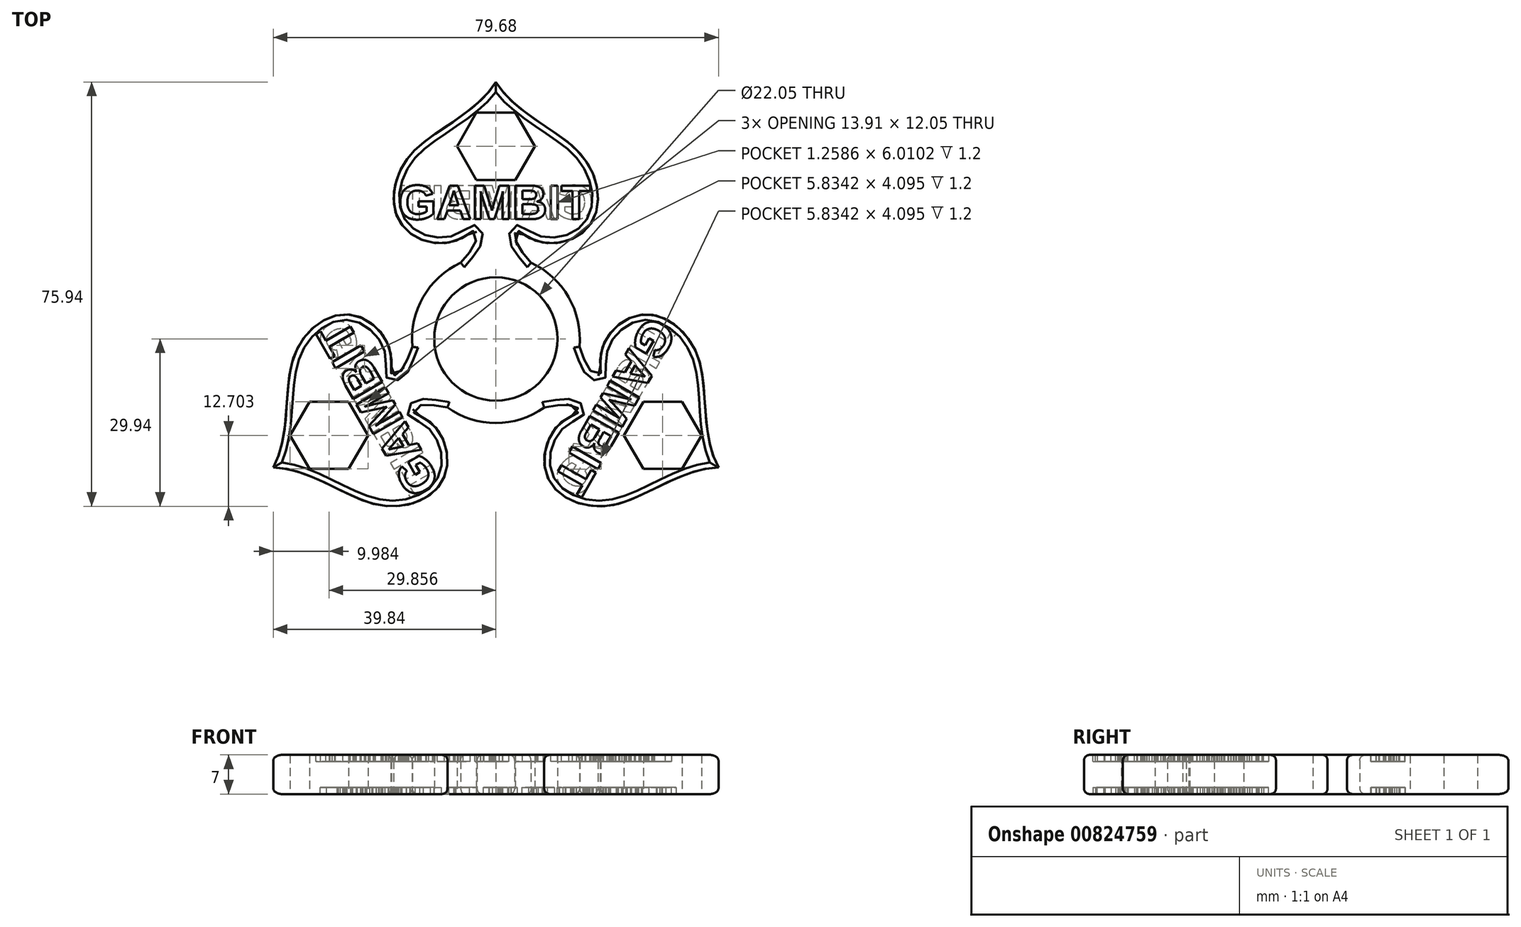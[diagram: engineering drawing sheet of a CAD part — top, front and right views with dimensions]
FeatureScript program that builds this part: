
annotation { "Feature Type Name" : "Feature", "Feature Type Description" : "" }
export const myFeature = defineFeature(function(context is Context, id is Id, definition is map)
    precondition{}
    {
        {
            var Q0;
            Q0=qCreatedBy(makeId("Top.planeOp"),FACE);
            var sketch = newSketch(context, id + "F0", { "sketchPlane" : qUnion([Q0])});
            skCircle(sketch, "E0", {"center": v(0, 0) * mm, "radius": 11.03 * mm});
            skCircle(sketch, "E1", {"center": v(0, 0) * mm, "radius": 15.03 * mm});
            skCircle(sketch, "E2", {"center": v(0, 0) * mm, "radius": 46 * mm, "construction": true});
            skLineSegment(sketch, "E3", {"start": v(0, 0) * mm, "end": v(0, 50.77) * mm, "construction": true});
            skFitSpline(sketch, "E4", {"points": [v(-6.29, 13.65) * mm, v(-3.78, 16.83) * mm, v(-3.57, 19.36) * mm, v(-6.6, 17.8) * mm, v(-13.45, 17.85) * mm, v(-17.97, 22.72) * mm, v(-15.15, 33.11) * mm, v(0, 46) * mm], "startDerivative": vector(35.72, 51.03) * mm, "endDerivative": vector(43.67, 71.8) * mm});
            skCircle(sketch, "E5", {"center": v(-9.97, 25.6) * mm, "radius": 8.5 * mm, "construction": true});
            skFitSpline(sketch, "E6.MirrorCS", {"points": [v(6.29, 13.65) * mm, v(3.78, 16.83) * mm, v(3.57, 19.36) * mm, v(6.6, 17.8) * mm, v(13.45, 17.85) * mm, v(17.97, 22.72) * mm, v(15.15, 33.11) * mm, v(0, 46) * mm], "startDerivative": vector(-35.72, 51.03) * mm, "endDerivative": vector(-43.67, 71.8) * mm});
            skCircle(sketch, "E7.cCircle", {"center": v(0, 34.47) * mm, "radius": 6.02 * mm, "construction": true});
            skLineSegment(sketch, "E7.0", {"start": v(3.48, 28.45) * mm, "end": v(-3.48, 28.45) * mm});
            skLineSegment(sketch, "E7.1", {"start": v(-3.48, 28.45) * mm, "end": v(-6.96, 34.47) * mm});
            skLineSegment(sketch, "E7.2", {"start": v(-6.96, 34.47) * mm, "end": v(-3.48, 40.5) * mm});
            skLineSegment(sketch, "E7.3", {"start": v(-3.48, 40.5) * mm, "end": v(3.48, 40.5) * mm});
            skLineSegment(sketch, "E7.4", {"start": v(3.48, 40.5) * mm, "end": v(6.96, 34.47) * mm});
            skLineSegment(sketch, "E7.5", {"start": v(6.96, 34.47) * mm, "end": v(3.48, 28.45) * mm});
            skPoint(sketch, "E7.0.midPoint", {"position": v(0, 28.45) * mm});
            skSolve(sketch);
        }
        {
            var Q0;
            {var subQ1=sQuery(id+"F0.wireOp",EDGE,"E4");Q0=makeQuery(id+"F0.imprint","IMPRINT",FACE,{"disambiguationData":[TD([[makeQuery(id+"F0.imprint","IMPRINT",EDGE,{"derivedFrom":subQ1}),-1.0]])]});}
            var Q1;
            Q1=makeQuery(id+"F0.imprint","IMPRINT",FACE,{"disambiguationData":[TD([[makeQuery(id+"F0.imprint","IMPRINT",EDGE,{"derivedFrom":sQuery(id+"F0.wireOp",EDGE,"E0")}),-1.0]])]});
            extrude(context, id + "F1", {"entities" : qUnion([Q0, Q1]), "depth" : 7 * mm, "offsetDistance" : 25 * mm});
        }
        {
            var Q0;
            Q0=qCreatedBy(makeId("Front.planeOp"),FACE);
            var sketch = newSketch(context, id + "F2", { "sketchPlane" : qUnion([Q0])});
            skLineSegment(sketch, "E8", {"start": v(0, 0) * mm, "end": v(0, 35.93) * mm, "construction": true});
            skSolve(sketch);
        }
        {
            var Q0;
            Q0=makeQuery(id+"F1.opExtrude","CAP_FACE",FACE,{"disambiguationData":[OSD([sQuery(id+"F0.wireOp",EDGE,"E0"),sQuery(id+"F0.wireOp",EDGE,"E1"),sQuery(id+"F0.wireOp",EDGE,"E4"),sQuery(id+"F0.wireOp",EDGE,"E6.MirrorCS"),sQuery(id+"F0.wireOp",EDGE,"E7.0"),sQuery(id+"F0.wireOp",EDGE,"E7.1"),sQuery(id+"F0.wireOp",EDGE,"E7.2"),sQuery(id+"F0.wireOp",EDGE,"E7.3"),sQuery(id+"F0.wireOp",EDGE,"E7.4"),sQuery(id+"F0.wireOp",EDGE,"E7.5")])],"isStart":false});
            var sketch = newSketch(context, id + "F3", { "sketchPlane" : qUnion([Q0])});
            skText(sketch, "E9", { "text": "GAMBIT\n", "fontName": "Arimo-Bold.ttf"});
            const initialGuessF3  = {"E9": [-0.01747, 0.02145, 1, 0, 0.00629]};
            skSetInitialGuess(sketch, initialGuessF3);
            skSolve(sketch);
        }
        {
            var Q0;
            Q0=makeQuery(id+"F3.imprint","IMPRINT",FACE,{"disambiguationData":[TD([[makeQuery(id+"F3.imprint","IMPRINT",EDGE,{"derivedFrom":sQuery(id+"F3.wireOp",EDGE,"E9.sketch_text.stroke-21")}),-1.0]])]});
            var Q1;
            Q1=makeQuery(id+"F3.imprint","IMPRINT",FACE,{"disambiguationData":[TD([[makeQuery(id+"F3.imprint","IMPRINT",EDGE,{"derivedFrom":sQuery(id+"F3.wireOp",EDGE,"E9.sketch_text.stroke-36")}),-1.0]])]});
            var Q2;
            Q2=makeQuery(id+"F3.imprint","IMPRINT",FACE,{"disambiguationData":[TD([[makeQuery(id+"F3.imprint","IMPRINT",EDGE,{"derivedFrom":sQuery(id+"F3.wireOp",EDGE,"E9.sketch_text.stroke-57")}),-1.0]])]});
            var Q3;
            Q3=makeQuery(id+"F3.imprint","IMPRINT",FACE,{"disambiguationData":[TD([[makeQuery(id+"F3.imprint","IMPRINT",EDGE,{"derivedFrom":sQuery(id+"F3.wireOp",EDGE,"E9.sketch_text.stroke-81")}),-1.0]])]});
            var Q4;
            Q4=makeQuery(id+"F3.imprint","IMPRINT",FACE,{"disambiguationData":[TD([[makeQuery(id+"F3.imprint","IMPRINT",EDGE,{"derivedFrom":sQuery(id+"F3.wireOp",EDGE,"E9.sketch_text.stroke-85")}),-1.0]])]});
            var Q5;
            Q5=makeQuery(id+"F3.imprint","IMPRINT",FACE,{"disambiguationData":[TD([[makeQuery(id+"F3.imprint","IMPRINT",EDGE,{"derivedFrom":sQuery(id+"F3.wireOp",EDGE,"E9.sketch_text.stroke-0")}),-1.0]])]});
            extrude(context, id + "F4", {"entities" : qUnion([Q0, Q1, Q2, Q3, Q4, Q5]), "operationType" : NewBodyOperationType.REMOVE, "oppositeDirection" : true, "depth" : 1.2 * mm, "offsetDistance" : 25 * mm});
        }
        {
            var Q0;
            Q0=makeQuery(id+"F1.opExtrude","CAP_FACE",FACE,{"disambiguationData":[OSD([sQuery(id+"F0.wireOp",EDGE,"E0"),sQuery(id+"F0.wireOp",EDGE,"E1"),sQuery(id+"F0.wireOp",EDGE,"E4"),sQuery(id+"F0.wireOp",EDGE,"E6.MirrorCS"),sQuery(id+"F0.wireOp",EDGE,"E7.0"),sQuery(id+"F0.wireOp",EDGE,"E7.1"),sQuery(id+"F0.wireOp",EDGE,"E7.2"),sQuery(id+"F0.wireOp",EDGE,"E7.3"),sQuery(id+"F0.wireOp",EDGE,"E7.4"),sQuery(id+"F0.wireOp",EDGE,"E7.5")])],"isStart":true});
            var sketch = newSketch(context, id + "F5", { "sketchPlane" : qUnion([Q0])});
            skText(sketch, "E10", { "text": "GAMBIT", "fontName": "Arimo-Bold.ttf"});
            const initialGuessF5  = {"E10": [0.01747, -0.02145, -1, 0, 0.00629]};
            skSetInitialGuess(sketch, initialGuessF5);
            skSolve(sketch);
        }
        {
            var Q0;
            Q0=makeQuery(id+"F5.imprint","IMPRINT",FACE,{"disambiguationData":[TD([[makeQuery(id+"F5.imprint","IMPRINT",EDGE,{"derivedFrom":sQuery(id+"F5.wireOp",EDGE,"E10.sketch_text.stroke-0")}),-1.0]])]});
            var Q1;
            Q1=makeQuery(id+"F5.imprint","IMPRINT",FACE,{"disambiguationData":[TD([[makeQuery(id+"F5.imprint","IMPRINT",EDGE,{"derivedFrom":sQuery(id+"F5.wireOp",EDGE,"E10.sketch_text.stroke-21")}),-1.0]])]});
            var Q2;
            Q2=makeQuery(id+"F5.imprint","IMPRINT",FACE,{"disambiguationData":[TD([[makeQuery(id+"F5.imprint","IMPRINT",EDGE,{"derivedFrom":sQuery(id+"F5.wireOp",EDGE,"E10.sketch_text.stroke-36")}),-1.0]])]});
            var Q3;
            Q3=makeQuery(id+"F5.imprint","IMPRINT",FACE,{"disambiguationData":[TD([[makeQuery(id+"F5.imprint","IMPRINT",EDGE,{"derivedFrom":sQuery(id+"F5.wireOp",EDGE,"E10.sketch_text.stroke-57")}),-1.0]])]});
            var Q4;
            Q4=makeQuery(id+"F5.imprint","IMPRINT",FACE,{"disambiguationData":[TD([[makeQuery(id+"F5.imprint","IMPRINT",EDGE,{"derivedFrom":sQuery(id+"F5.wireOp",EDGE,"E10.sketch_text.stroke-81")}),-1.0]])]});
            var Q5;
            Q5=makeQuery(id+"F5.imprint","IMPRINT",FACE,{"disambiguationData":[TD([[makeQuery(id+"F5.imprint","IMPRINT",EDGE,{"derivedFrom":sQuery(id+"F5.wireOp",EDGE,"E10.sketch_text.stroke-85")}),-1.0]])]});
            extrude(context, id + "F6", {"entities" : qUnion([Q0, Q1, Q2, Q3, Q4, Q5]), "operationType" : NewBodyOperationType.REMOVE, "oppositeDirection" : true, "depth" : 1.2 * mm, "offsetDistance" : 25 * mm});
        }
        {
            var Q0;
            {var subQ0=sQuery(id+"F0.wireOp",EDGE,"E4");var subQ1=makeQuery(id+"F1.opExtrude","SWEPT_FACE",FACE,{"disambiguationData":[OSD([subQ0])]});var subQ4=sQuery(id+"F0.wireOp",EDGE,"E1");Q0=makeQuery(id+"F9.boolean.opBoolean","SPLIT",EDGE,{"disambiguationData":[TD([subQ1])],"derivedFrom":makeQuery(id+"F1.opExtrude","CAP_EDGE",EDGE,{"disambiguationData":[OSD([subQ4])],"isStart":false})});}
            var Q1;
            {var subQ5=sQuery(id+"F0.wireOp",EDGE,"E1");var subQ7=sQuery(id+"F0.wireOp",EDGE,"E4");var subQ8=makeQuery(id+"F1.opExtrude","SWEPT_FACE",FACE,{"disambiguationData":[OSD([subQ7])]});Q1=makeQuery(id+"F9.boolean.opBoolean","SPLIT",EDGE,{"disambiguationData":[TD([makeQuery(id+"F9.opPattern","COPY",FACE,{"derivedFrom":subQ8,"instanceName":"1"})])],"derivedFrom":makeQuery(id+"F1.opExtrude","CAP_EDGE",EDGE,{"disambiguationData":[OSD([subQ5])],"isStart":false})});}
            var Q2;
            {var subQ3=sQuery(id+"F0.wireOp",EDGE,"E6.MirrorCS");var subQ4=makeQuery(id+"F1.opExtrude","SWEPT_FACE",FACE,{"disambiguationData":[OSD([subQ3])]});var subQ5=sQuery(id+"F0.wireOp",EDGE,"E1");Q2=makeQuery(id+"F9.boolean.opBoolean","SPLIT",EDGE,{"disambiguationData":[TD([subQ4])],"derivedFrom":makeQuery(id+"F1.opExtrude","CAP_EDGE",EDGE,{"disambiguationData":[OSD([subQ5])],"isStart":false})});}
            var Q3;
            {var subQ7=sQuery(id+"F0.wireOp",EDGE,"E6.MirrorCS");var subQ8=makeQuery(id+"F1.opExtrude","SWEPT_FACE",FACE,{"disambiguationData":[OSD([subQ7])]});var subQ9=sQuery(id+"F0.wireOp",EDGE,"E1");Q3=makeQuery(id+"F9.boolean.opBoolean","SPLIT",EDGE,{"disambiguationData":[TD([subQ8])],"derivedFrom":makeQuery(id+"F1.opExtrude","CAP_EDGE",EDGE,{"disambiguationData":[OSD([subQ9])],"isStart":true})});}
            var Q4;
            {var subQ0=sQuery(id+"F0.wireOp",EDGE,"E4");var subQ1=makeQuery(id+"F1.opExtrude","SWEPT_FACE",FACE,{"disambiguationData":[OSD([subQ0])]});var subQ11=sQuery(id+"F0.wireOp",EDGE,"E1");Q4=makeQuery(id+"F9.boolean.opBoolean","SPLIT",EDGE,{"disambiguationData":[TD([subQ1])],"derivedFrom":makeQuery(id+"F1.opExtrude","CAP_EDGE",EDGE,{"disambiguationData":[OSD([subQ11])],"isStart":true})});}
            var Q5;
            {var subQ9=sQuery(id+"F0.wireOp",EDGE,"E1");var subQ11=sQuery(id+"F0.wireOp",EDGE,"E4");var subQ12=makeQuery(id+"F1.opExtrude","SWEPT_FACE",FACE,{"disambiguationData":[OSD([subQ11])]});Q5=makeQuery(id+"F9.boolean.opBoolean","SPLIT",EDGE,{"disambiguationData":[TD([makeQuery(id+"F9.opPattern","COPY",FACE,{"derivedFrom":subQ12,"instanceName":"1"})])],"derivedFrom":makeQuery(id+"F1.opExtrude","CAP_EDGE",EDGE,{"disambiguationData":[OSD([subQ9])],"isStart":true})});}
            fillet(context, id + "F7", {"entities" : qUnion([Q0, Q1, Q2, Q3, Q4, Q5]), "radius" : 1 * mm, "tangentPropagation" : true, "allowEdgeOverflow" : false});
        }
        {
            var Q0;
            Q0=makeQuery(id+"F1.opExtrude","CAP_EDGE",EDGE,{"disambiguationData":[OSD([sQuery(id+"F0.wireOp",EDGE,"E6.MirrorCS")])],"isStart":false});
            var Q1;
            Q1=makeQuery(id+"F1.opExtrude","CAP_EDGE",EDGE,{"disambiguationData":[OSD([sQuery(id+"F0.wireOp",EDGE,"E6.MirrorCS")])],"isStart":true});
            var Q2;
            Q2=makeQuery(id+"F1.opExtrude","CAP_EDGE",EDGE,{"disambiguationData":[OSD([sQuery(id+"F0.wireOp",EDGE,"E4")])],"isStart":true});
            var Q3;
            Q3=makeQuery(id+"F1.opExtrude","CAP_EDGE",EDGE,{"disambiguationData":[OSD([sQuery(id+"F0.wireOp",EDGE,"E4")])],"isStart":false});
            fillet(context, id + "F8", {"entities" : qUnion([Q0, Q1, Q2, Q3]), "radius" : 1 * mm, "tangentPropagation" : true, "allowEdgeOverflow" : false});
        }
        {
            var Q0;
            Q0=makeQuery(id+"F1.opExtrude","SWEPT_BODY",BODY,{"disambiguationData":[OSD([sQuery(id+"F0.wireOp",EDGE,"E0"),sQuery(id+"F0.wireOp",EDGE,"E1"),sQuery(id+"F0.wireOp",EDGE,"E4"),sQuery(id+"F0.wireOp",EDGE,"E6.MirrorCS"),sQuery(id+"F0.wireOp",EDGE,"E7.0"),sQuery(id+"F0.wireOp",EDGE,"E7.1"),sQuery(id+"F0.wireOp",EDGE,"E7.2"),sQuery(id+"F0.wireOp",EDGE,"E7.3"),sQuery(id+"F0.wireOp",EDGE,"E7.4"),sQuery(id+"F0.wireOp",EDGE,"E7.5")])]});
            var Q1;
            Q1=sQuery(id+"F2.wireOp",EDGE,"E8");
            circularPattern(context, id + "F9", {"operationType" : NewBodyOperationType.ADD, "entities" : qUnion([Q0]), "axis" : qUnion([Q1]), "angle" : 360 * degree, "instanceCount" : 3, "equalSpace" : true});
        }
    });
